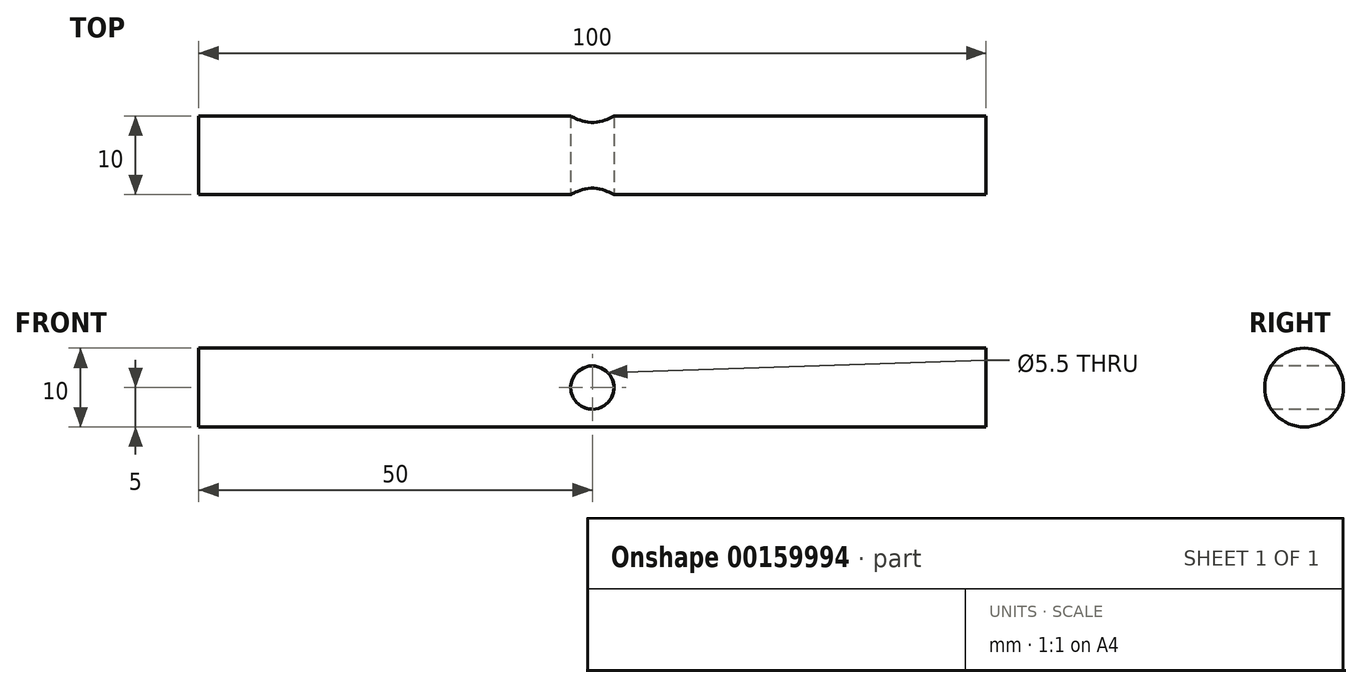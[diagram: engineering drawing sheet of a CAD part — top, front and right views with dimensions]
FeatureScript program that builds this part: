
annotation { "Feature Type Name" : "Feature", "Feature Type Description" : "" }
export const myFeature = defineFeature(function(context is Context, id is Id, definition is map)
    precondition{}
    {
        {
            var Q0;
            Q0=qCreatedBy(makeId("Right.planeOp"),FACE);
            var sketch = newSketch(context, id + "F0", { "sketchPlane" : qUnion([Q0])});
            skCircle(sketch, "E0", {"center": v(0, 0) * mm, "radius": 5 * mm});
            skSolve(sketch);
        }
        {
            var Q0;
            Q0=makeQuery(id+"F0.imprint","IMPRINT",FACE,{"disambiguationData":[TD([[makeQuery(id+"F0.imprint","IMPRINT",EDGE,{"derivedFrom":sQuery(id+"F0.wireOp",EDGE,"E0")}),1.0]])]});
            extrude(context, id + "F1", {"entities" : qUnion([Q0]), "depth" : 100 * mm});
        }
        {
            var Q0;
            Q0=qCreatedBy(makeId("Front.planeOp"),FACE);
            var sketch = newSketch(context, id + "F2", { "sketchPlane" : qUnion([Q0])});
            skCircle(sketch, "E1", {"center": v(50, 0) * mm, "radius": 2.75 * mm});
            skSolve(sketch);
        }
        {
            var Q0;
            Q0=makeQuery(id+"F2.imprint","IMPRINT",FACE,{"disambiguationData":[TD([[makeQuery(id+"F2.imprint","IMPRINT",EDGE,{"derivedFrom":sQuery(id+"F2.wireOp",EDGE,"E1")}),1.0]])]});
            extrude(context, id + "F3", {"entities" : qUnion([Q0]), "operationType" : NewBodyOperationType.REMOVE, "endBound" : BoundingType.THROUGH_ALL, "oppositeDirection" : true, "depth" : 25 * mm, "hasSecondDirection" : true, "secondDirectionOppositeDirection" : false, "secondDirectionDepth" : 25 * mm});
        }
    });
